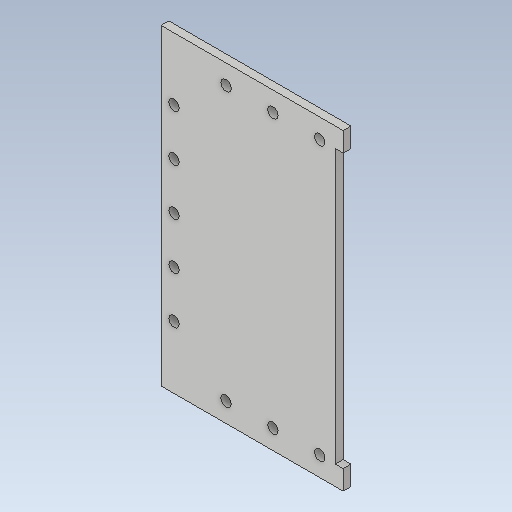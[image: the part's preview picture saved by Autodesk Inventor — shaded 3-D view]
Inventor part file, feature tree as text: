
AUTODESK INVENTOR PART (.ipt)
format: ipt  version: 2020 (Build 240168000, 168)  size: 113,664 bytes
history: native  units: mm
features: other x2, extrude x1, sketch x1, reference x1
ambient origin geometry x8: Origin, YZ Plane, XZ Plane, XY Plane, X Axis, Y Axis, Z Axis, Center Point
bodies: Body1 (feature_tree)
feature tree (5):
  extrude  "Extrusion2"  [1 undecoded]
  sketch  "Sketch3"  dims[d9=3.0mm d10=0.0mm]
  reference  "Reference5"
  other  "КВ33.000.100 - Блок переключение передач.iam"
  other  "КВ33.000.101 - Площадка крепежная:1"
note: 1 required parameter value undecoded (feature->parameter linkage not recoverable at this tier; creation-order binding heuristic only, values carry confidence <= 0.55)
